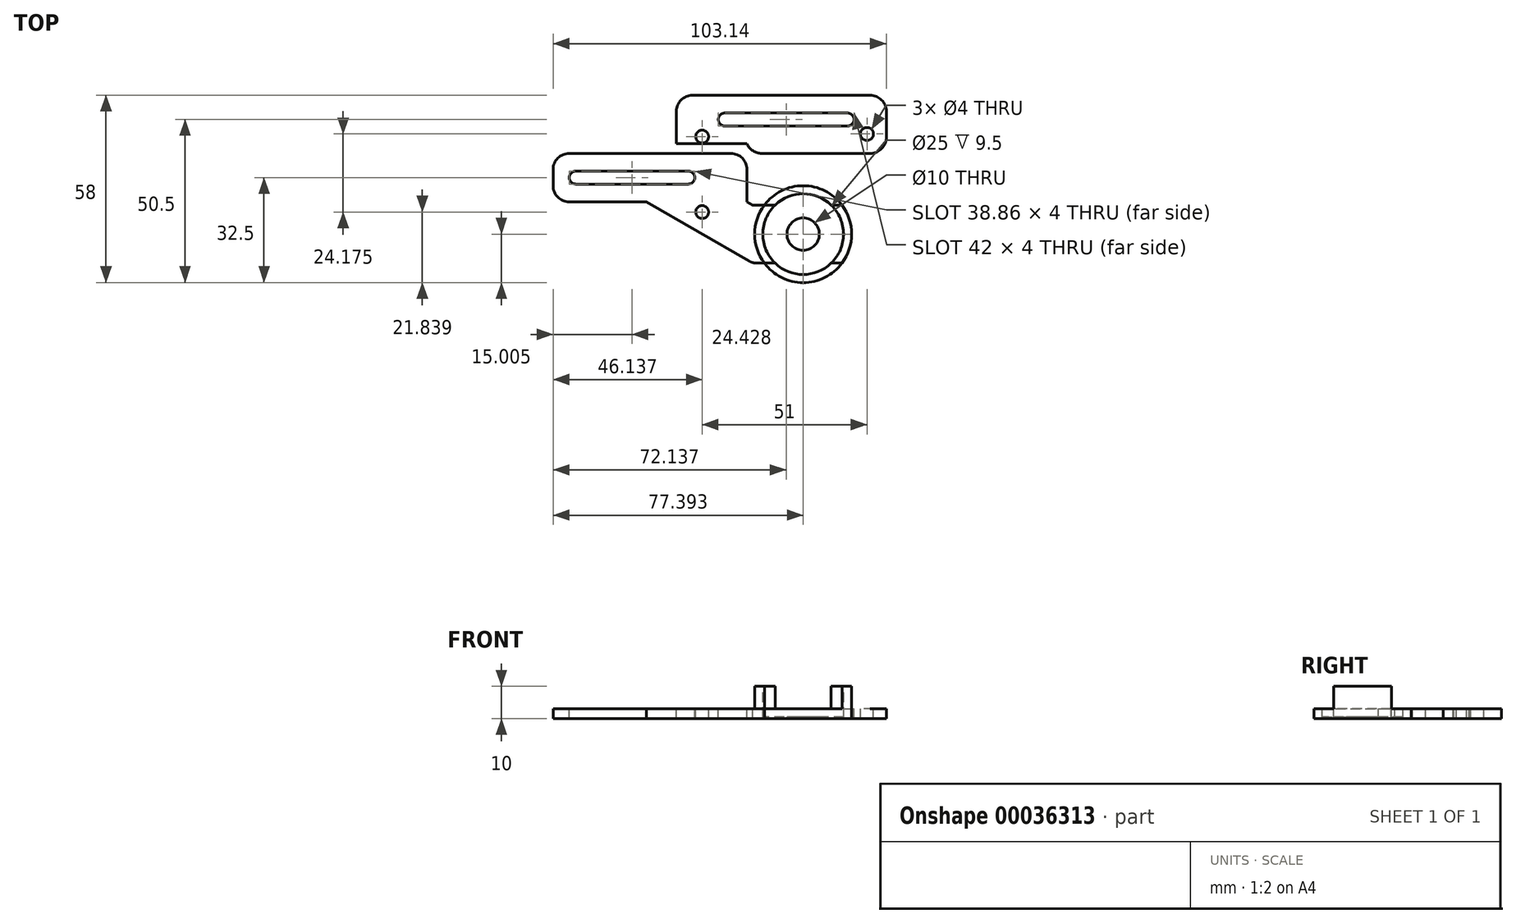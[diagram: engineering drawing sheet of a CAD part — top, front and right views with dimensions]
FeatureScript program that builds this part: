
annotation { "Feature Type Name" : "Feature", "Feature Type Description" : "" }
export const myFeature = defineFeature(function(context is Context, id is Id, definition is map)
    precondition{}
    {
        {
            var Q0;
            Q0=qCreatedBy(makeId("Top.planeOp"),FACE);
            var sketch = newSketch(context, id + "F0", { "sketchPlane" : qUnion([Q0])});
            skLineSegment(sketch, "E0.bottom", {"start": v(-30, 15) * mm, "end": v(30, 15) * mm});
            skLineSegment(sketch, "E0.top", {"start": v(-30, 0) * mm, "end": v(30, 0) * mm});
            skLineSegment(sketch, "E0.left", {"start": v(-30, 15) * mm, "end": v(-30, 0) * mm});
            skLineSegment(sketch, "E0.right", {"start": v(30, 15) * mm, "end": v(30, 0) * mm});
            skLineSegment(sketch, "E1", {"start": v(0, 0) * mm, "end": v(0, 15) * mm, "construction": true});
            skCircle(sketch, "E2", {"center": v(47.4, -10) * mm, "radius": 15 * mm});
            skLineSegment(sketch, "E3.left", {"start": v(31.72, -1) * mm, "end": v(31.72, -19) * mm});
            skLineSegment(sketch, "E3.right", {"start": v(47.4, -1) * mm, "end": v(47.4, -19) * mm});
            skCircle(sketch, "E4", {"center": v(47.4, -10) * mm, "radius": 12.5 * mm});
            skLineSegment(sketch, "E5", {"start": v(47.4, -10) * mm, "end": v(31.72, -10) * mm, "construction": true});
            skLineSegment(sketch, "E6", {"start": v(47.4, -1) * mm, "end": v(56.07, -1) * mm});
            skLineSegment(sketch, "E7", {"start": v(56.07, -1) * mm, "end": v(59.4, -1) * mm});
            skLineSegment(sketch, "E8", {"start": v(47.4, -19) * mm, "end": v(56.07, -19) * mm});
            skLineSegment(sketch, "E9", {"start": v(56.07, -19) * mm, "end": v(59.4, -19) * mm});
            skLineSegment(sketch, "E10", {"start": v(47.4, -1) * mm, "end": v(38.72, -1) * mm});
            skLineSegment(sketch, "E11", {"start": v(38.72, -1) * mm, "end": v(35.4, -1) * mm});
            skLineSegment(sketch, "E12", {"start": v(35.4, -1) * mm, "end": v(31.72, -1) * mm});
            skLineSegment(sketch, "E13", {"start": v(47.4, -19) * mm, "end": v(38.72, -19) * mm});
            skLineSegment(sketch, "E14", {"start": v(38.72, -19) * mm, "end": v(35.4, -19) * mm});
            skLineSegment(sketch, "E15", {"start": v(35.4, -19) * mm, "end": v(31.72, -19) * mm});
            skLineSegment(sketch, "E16", {"start": v(-30, 7.5) * mm, "end": v(0, 7.5) * mm, "construction": true});
            skLineSegment(sketch, "E17", {"start": v(0, 7.5) * mm, "end": v(30, 7.5) * mm, "construction": true});
            skLineSegment(sketch, "E18", {"start": v(-10, 7.5) * mm, "end": v(47.4, -10) * mm, "construction": true});
            skLineSegment(sketch, "E19", {"start": v(31.72, -19) * mm, "end": v(-1.15, 0) * mm});
            skLineSegment(sketch, "E20", {"start": v(31.72, -1) * mm, "end": v(30, 0) * mm});
            skLineSegment(sketch, "E21.bottom", {"start": v(30, 15) * mm, "end": v(8.14, 15) * mm});
            skLineSegment(sketch, "E21.top", {"start": v(30, 18) * mm, "end": v(8.14, 18) * mm});
            skLineSegment(sketch, "E21.left", {"start": v(30, 15) * mm, "end": v(30, 18) * mm});
            skLineSegment(sketch, "E21.right", {"start": v(8.14, 15) * mm, "end": v(8.14, 18) * mm});
            skLineSegment(sketch, "E22.bottom", {"start": v(8.14, 18) * mm, "end": v(73.14, 18) * mm});
            skLineSegment(sketch, "E22.top", {"start": v(8.14, 33) * mm, "end": v(73.14, 33) * mm});
            skLineSegment(sketch, "E22.left", {"start": v(8.14, 18) * mm, "end": v(8.14, 33) * mm});
            skLineSegment(sketch, "E22.right", {"start": v(73.14, 18) * mm, "end": v(73.14, 33) * mm});
            skCircle(sketch, "E23", {"center": v(-23, 7.5) * mm, "radius": 2 * mm});
            skCircle(sketch, "E24", {"center": v(11.86, 7.5) * mm, "radius": 2 * mm});
            skLineSegment(sketch, "E25", {"start": v(40.64, 33) * mm, "end": v(40.64, 25.5) * mm});
            skLineSegment(sketch, "E26", {"start": v(40.64, 25.5) * mm, "end": v(40.64, 18) * mm});
            skLineSegment(sketch, "E27", {"start": v(8.14, 25.5) * mm, "end": v(40.64, 25.5) * mm, "construction": true});
            skLineSegment(sketch, "E28", {"start": v(40.64, 25.5) * mm, "end": v(73.14, 25.5) * mm, "construction": true});
            skCircle(sketch, "E29", {"center": v(61.14, 25.5) * mm, "radius": 2 * mm});
            skCircle(sketch, "E30", {"center": v(23.14, 25.5) * mm, "radius": 2 * mm});
            skLineSegment(sketch, "E31", {"start": v(11.86, 7.5) * mm, "end": v(11.86, 9.5) * mm});
            skLineSegment(sketch, "E32", {"start": v(11.86, 7.5) * mm, "end": v(11.86, 5.5) * mm});
            skLineSegment(sketch, "E33", {"start": v(11.86, 5.5) * mm, "end": v(-23, 5.5) * mm});
            skLineSegment(sketch, "E34", {"start": v(-23, 5.5) * mm, "end": v(-23, 7.5) * mm});
            skLineSegment(sketch, "E35", {"start": v(11.86, 9.5) * mm, "end": v(-23, 9.5) * mm});
            skLineSegment(sketch, "E36", {"start": v(-23, 9.5) * mm, "end": v(-23, 7.5) * mm});
            skLineSegment(sketch, "E37", {"start": v(23.14, 25.5) * mm, "end": v(23.14, 23.5) * mm});
            skLineSegment(sketch, "E38", {"start": v(61.14, 23.5) * mm, "end": v(61.14, 25.5) * mm});
            skLineSegment(sketch, "E39", {"start": v(23.14, 25.5) * mm, "end": v(23.14, 27.5) * mm});
            skLineSegment(sketch, "E40", {"start": v(61.14, 27.5) * mm, "end": v(61.14, 25.5) * mm});
            skLineSegment(sketch, "E41", {"start": v(23.14, 23.5) * mm, "end": v(61.14, 23.5) * mm});
            skLineSegment(sketch, "E42", {"start": v(61.14, 27.5) * mm, "end": v(23.14, 27.5) * mm});
            skLineSegment(sketch, "E43", {"start": v(30, 15) * mm, "end": v(73.14, 15) * mm});
            skLineSegment(sketch, "E44", {"start": v(73.14, 15) * mm, "end": v(73.14, 18) * mm});
            skCircle(sketch, "E45", {"center": v(16.14, 20.22) * mm, "radius": 2 * mm});
            skCircle(sketch, "E46", {"center": v(67.14, 21.01) * mm, "radius": 2 * mm});
            skCircle(sketch, "E47", {"center": v(16.14, -3.16) * mm, "radius": 2 * mm});
            skSolve(sketch);
        }
        {
            var Q0;
            Q0=makeQuery(id+"F0.imprint","IMPRINT",FACE,{"disambiguationData":[TD([[makeQuery(id+"F0.imprint","IMPRINT",EDGE,{"derivedFrom":sQuery(id+"F0.wireOp",EDGE,"E3.right")}),-1.0]])]});
            var sketch = newSketch(context, id + "F1", { "sketchPlane" : qUnion([Q0])});
            skCircle(sketch, "E48", {"center": v(47.4, -10) * mm, "radius": 5 * mm});
            skSolve(sketch);
        }
        {
            var Q0;
            Q0=makeQuery(id+"F0.imprint","IMPRINT",FACE,{"disambiguationData":[TD([[makeQuery(id+"F0.imprint","IMPRINT",EDGE,{"derivedFrom":sQuery(id+"F0.wireOp",EDGE,"E0.bottom")}),-1.0]])]});
            var Q1;
            Q1=makeQuery(id+"F0.imprint","IMPRINT",FACE,{"disambiguationData":[TD([[makeQuery(id+"F0.imprint","IMPRINT",EDGE,{"derivedFrom":sQuery(id+"F0.wireOp",EDGE,"E3.left")}),-1.0]])]});
            var Q2;
            Q2=makeQuery(id+"F0.imprint","IMPRINT",FACE,{"disambiguationData":[TD([[makeQuery(id+"F0.imprint","IMPRINT",EDGE,{"derivedFrom":sQuery(id+"F0.wireOp",EDGE,"E22.top")}),-1.0]])]});
            var Q3;
            Q3=makeQuery(id+"F0.imprint","IMPRINT",FACE,{"disambiguationData":[TD([[makeQuery(id+"F0.imprint","IMPRINT",EDGE,{"derivedFrom":sQuery(id+"F0.wireOp",EDGE,"E21.bottom")}),-1.0]])]});
            var Q4;
            Q4=makeQuery(id+"F0.imprint","IMPRINT",FACE,{"disambiguationData":[TD([[makeQuery(id+"F0.imprint","IMPRINT",EDGE,{"derivedFrom":sQuery(id+"F0.wireOp",EDGE,"E3.left")}),1.0]])]});
            var Q5;
            {var subQ1=sQuery(id+"F0.wireOp",EDGE,"E11");Q5=makeQuery(id+"F0.imprint","IMPRINT",FACE,{"disambiguationData":[TD([[makeQuery(id+"F0.imprint","IMPRINT",EDGE,{"derivedFrom":subQ1}),1.0]])]});}
            var Q6;
            Q6=makeQuery(id+"F0.imprint","IMPRINT",FACE,{"disambiguationData":[TD([[makeQuery(id+"F0.imprint","IMPRINT",EDGE,{"derivedFrom":sQuery(id+"F0.wireOp",EDGE,"E3.right")}),-1.0]])]});
            var Q7;
            {var subQ1=sQuery(id+"F0.wireOp",EDGE,"E6");Q7=makeQuery(id+"F0.imprint","IMPRINT",FACE,{"disambiguationData":[TD([[makeQuery(id+"F0.imprint","IMPRINT",EDGE,{"derivedFrom":subQ1}),1.0]])]});}
            var Q8;
            Q8=makeQuery(id+"F0.imprint","IMPRINT",FACE,{"disambiguationData":[TD([[makeQuery(id+"F0.imprint","IMPRINT",EDGE,{"derivedFrom":sQuery(id+"F0.wireOp",EDGE,"E3.right")}),1.0]])]});
            var Q9;
            {var subQ1=sQuery(id+"F0.wireOp",EDGE,"E7");Q9=makeQuery(id+"F0.imprint","IMPRINT",FACE,{"disambiguationData":[TD([[makeQuery(id+"F0.imprint","IMPRINT",EDGE,{"derivedFrom":subQ1}),-1.0]])]});}
            var Q10;
            {var subQ1=sQuery(id+"F0.wireOp",EDGE,"E9");Q10=makeQuery(id+"F0.imprint","IMPRINT",FACE,{"disambiguationData":[TD([[makeQuery(id+"F0.imprint","IMPRINT",EDGE,{"derivedFrom":subQ1}),-1.0]])]});}
            var Q11;
            {var subQ1=sQuery(id+"F0.wireOp",EDGE,"E8");Q11=makeQuery(id+"F0.imprint","IMPRINT",FACE,{"disambiguationData":[TD([[makeQuery(id+"F0.imprint","IMPRINT",EDGE,{"derivedFrom":subQ1}),-1.0]])]});}
            var Q12;
            {var subQ1=sQuery(id+"F0.wireOp",EDGE,"E7");Q12=makeQuery(id+"F0.imprint","IMPRINT",FACE,{"disambiguationData":[TD([[makeQuery(id+"F0.imprint","IMPRINT",EDGE,{"derivedFrom":subQ1}),1.0]])]});}
            var Q13;
            {var subQ1=sQuery(id+"F0.wireOp",EDGE,"E33");Q13=makeQuery(id+"F0.imprint","IMPRINT",FACE,{"disambiguationData":[TD([[makeQuery(id+"F0.imprint","IMPRINT",EDGE,{"derivedFrom":subQ1}),-1.0]])]});}
            var Q14;
            {var subQ1=sQuery(id+"F0.wireOp",EDGE,"E31");Q14=makeQuery(id+"F0.imprint","IMPRINT",FACE,{"disambiguationData":[TD([[makeQuery(id+"F0.imprint","IMPRINT",EDGE,{"derivedFrom":subQ1}),1.0]])]});}
            var Q15;
            {var subQ1=sQuery(id+"F0.wireOp",EDGE,"E31");Q15=makeQuery(id+"F0.imprint","IMPRINT",FACE,{"disambiguationData":[TD([[makeQuery(id+"F0.imprint","IMPRINT",EDGE,{"derivedFrom":subQ1}),-1.0]])]});}
            var Q16;
            {var subQ1=sQuery(id+"F0.wireOp",EDGE,"E34");Q16=makeQuery(id+"F0.imprint","IMPRINT",FACE,{"disambiguationData":[TD([[makeQuery(id+"F0.imprint","IMPRINT",EDGE,{"derivedFrom":subQ1}),1.0]])]});}
            var Q17;
            {var subQ1=sQuery(id+"F0.wireOp",EDGE,"E34");Q17=makeQuery(id+"F0.imprint","IMPRINT",FACE,{"disambiguationData":[TD([[makeQuery(id+"F0.imprint","IMPRINT",EDGE,{"derivedFrom":subQ1}),-1.0]])]});}
            var Q18;
            {var subQ1=sQuery(id+"F0.wireOp",EDGE,"E37");Q18=makeQuery(id+"F0.imprint","IMPRINT",FACE,{"disambiguationData":[TD([[makeQuery(id+"F0.imprint","IMPRINT",EDGE,{"derivedFrom":subQ1}),-1.0]])]});}
            var Q19;
            {var subQ1=sQuery(id+"F0.wireOp",EDGE,"E37");Q19=makeQuery(id+"F0.imprint","IMPRINT",FACE,{"disambiguationData":[TD([[makeQuery(id+"F0.imprint","IMPRINT",EDGE,{"derivedFrom":subQ1}),1.0]])]});}
            var Q20;
            {var subQ1=sQuery(id+"F0.wireOp",EDGE,"E41");Q20=makeQuery(id+"F0.imprint","IMPRINT",FACE,{"disambiguationData":[TD([[makeQuery(id+"F0.imprint","IMPRINT",EDGE,{"derivedFrom":subQ1}),1.0]])]});}
            var Q21;
            {var subQ1=sQuery(id+"F0.wireOp",EDGE,"E38");Q21=makeQuery(id+"F0.imprint","IMPRINT",FACE,{"disambiguationData":[TD([[makeQuery(id+"F0.imprint","IMPRINT",EDGE,{"derivedFrom":subQ1}),1.0]])]});}
            var Q22;
            {var subQ1=sQuery(id+"F0.wireOp",EDGE,"E38");Q22=makeQuery(id+"F0.imprint","IMPRINT",FACE,{"disambiguationData":[TD([[makeQuery(id+"F0.imprint","IMPRINT",EDGE,{"derivedFrom":subQ1}),-1.0]])]});}
            var Q23;
            {var subQ13=sQuery(id+"F0.wireOp",EDGE,"E22.left");Q23=makeQuery(id+"F0.imprint","IMPRINT",FACE,{"disambiguationData":[TD([[makeQuery(id+"F0.imprint","IMPRINT",EDGE,{"derivedFrom":subQ13}),-1.0]])]});}
            var Q24;
            {var subQ3=sQuery(id+"F0.wireOp",EDGE,"E21.left");Q24=makeQuery(id+"F0.imprint","IMPRINT",FACE,{"disambiguationData":[TD([[makeQuery(id+"F0.imprint","IMPRINT",EDGE,{"derivedFrom":subQ3}),-1.0]])]});}
            extrude(context, id + "F2", {"entities" : qUnion([Q0, Q1, Q2, Q3, Q4, Q5, Q6, Q7, Q8, Q9, Q10, Q11, Q12, Q13, Q14, Q15, Q16, Q17, Q18, Q19, Q20, Q21, Q22, Q23, Q24]), "oppositeDirection" : true, "depth" : 3 * mm});
        }
        {
            var Q0;
            {var subQ1=sQuery(id+"F0.wireOp",EDGE,"E6");Q0=makeQuery(id+"F0.imprint","IMPRINT",FACE,{"disambiguationData":[TD([[makeQuery(id+"F0.imprint","IMPRINT",EDGE,{"derivedFrom":subQ1}),1.0]])]});}
            var Q1;
            Q1=makeQuery(id+"F0.imprint","IMPRINT",FACE,{"disambiguationData":[TD([[makeQuery(id+"F0.imprint","IMPRINT",EDGE,{"derivedFrom":sQuery(id+"F0.wireOp",EDGE,"E3.right")}),-1.0]])]});
            var Q2;
            Q2=makeQuery(id+"F0.imprint","IMPRINT",FACE,{"disambiguationData":[TD([[makeQuery(id+"F0.imprint","IMPRINT",EDGE,{"derivedFrom":sQuery(id+"F0.wireOp",EDGE,"E3.right")}),1.0]])]});
            var Q3;
            {var subQ1=sQuery(id+"F0.wireOp",EDGE,"E8");Q3=makeQuery(id+"F0.imprint","IMPRINT",FACE,{"disambiguationData":[TD([[makeQuery(id+"F0.imprint","IMPRINT",EDGE,{"derivedFrom":subQ1}),-1.0]])]});}
            extrude(context, id + "F3", {"entities" : qUnion([Q0, Q1, Q2, Q3]), "operationType" : NewBodyOperationType.REMOVE, "oppositeDirection" : true, "depth" : 2.5 * mm});
        }
        {
            var Q0;
            {var subQ0=makeQuery(id+"F0.imprint","IMPRINT",EDGE,{"derivedFrom":sQuery(id+"F0.wireOp",EDGE,"E3.right")});var subQ1=sQuery(id+"F1.wireOp",EDGE,"E48");var subQ3=makeQuery(id+"F1.imprint","INTERSECT",VERTEX,{"disambiguationData":[OD(0.0)],"derivedFrom":[subQ0,subQ1]});Q0=makeQuery(id+"F1.imprint","IMPRINT",FACE,{"disambiguationData":[TD([[makeQuery(id+"F1.imprint","IMPRINT",EDGE,{"disambiguationData":[TD([[subQ3,-1.0]])],"derivedFrom":subQ1}),1.0]])]});}
            var Q1;
            {var subQ0=makeQuery(id+"F0.imprint","IMPRINT",EDGE,{"derivedFrom":sQuery(id+"F0.wireOp",EDGE,"E3.right")});var subQ1=sQuery(id+"F1.wireOp",EDGE,"E48");var subQ3=makeQuery(id+"F1.imprint","INTERSECT",VERTEX,{"disambiguationData":[OD(0.0)],"derivedFrom":[subQ0,subQ1]});Q1=makeQuery(id+"F1.imprint","IMPRINT",FACE,{"disambiguationData":[TD([[makeQuery(id+"F1.imprint","IMPRINT",EDGE,{"disambiguationData":[TD([[subQ3,1.0]])],"derivedFrom":subQ1}),1.0]])]});}
            extrude(context, id + "F4", {"entities" : qUnion([Q0, Q1]), "operationType" : NewBodyOperationType.REMOVE, "endBound" : BoundingType.THROUGH_ALL, "oppositeDirection" : true, "depth" : 25 * mm});
        }
        {
            var Q0;
            {var subQ1=sQuery(id+"F0.wireOp",EDGE,"E37");Q0=makeQuery(id+"F0.imprint","IMPRINT",FACE,{"disambiguationData":[TD([[makeQuery(id+"F0.imprint","IMPRINT",EDGE,{"derivedFrom":subQ1}),-1.0]])]});}
            var Q1;
            {var subQ1=sQuery(id+"F0.wireOp",EDGE,"E37");Q1=makeQuery(id+"F0.imprint","IMPRINT",FACE,{"disambiguationData":[TD([[makeQuery(id+"F0.imprint","IMPRINT",EDGE,{"derivedFrom":subQ1}),1.0]])]});}
            var Q2;
            {var subQ1=sQuery(id+"F0.wireOp",EDGE,"E41");Q2=makeQuery(id+"F0.imprint","IMPRINT",FACE,{"disambiguationData":[TD([[makeQuery(id+"F0.imprint","IMPRINT",EDGE,{"derivedFrom":subQ1}),1.0]])]});}
            var Q3;
            {var subQ1=sQuery(id+"F0.wireOp",EDGE,"E38");Q3=makeQuery(id+"F0.imprint","IMPRINT",FACE,{"disambiguationData":[TD([[makeQuery(id+"F0.imprint","IMPRINT",EDGE,{"derivedFrom":subQ1}),1.0]])]});}
            var Q4;
            {var subQ1=sQuery(id+"F0.wireOp",EDGE,"E38");Q4=makeQuery(id+"F0.imprint","IMPRINT",FACE,{"disambiguationData":[TD([[makeQuery(id+"F0.imprint","IMPRINT",EDGE,{"derivedFrom":subQ1}),-1.0]])]});}
            var Q5;
            {var subQ1=sQuery(id+"F0.wireOp",EDGE,"E31");Q5=makeQuery(id+"F0.imprint","IMPRINT",FACE,{"disambiguationData":[TD([[makeQuery(id+"F0.imprint","IMPRINT",EDGE,{"derivedFrom":subQ1}),-1.0]])]});}
            var Q6;
            {var subQ1=sQuery(id+"F0.wireOp",EDGE,"E31");Q6=makeQuery(id+"F0.imprint","IMPRINT",FACE,{"disambiguationData":[TD([[makeQuery(id+"F0.imprint","IMPRINT",EDGE,{"derivedFrom":subQ1}),1.0]])]});}
            var Q7;
            {var subQ1=sQuery(id+"F0.wireOp",EDGE,"E33");Q7=makeQuery(id+"F0.imprint","IMPRINT",FACE,{"disambiguationData":[TD([[makeQuery(id+"F0.imprint","IMPRINT",EDGE,{"derivedFrom":subQ1}),-1.0]])]});}
            var Q8;
            {var subQ1=sQuery(id+"F0.wireOp",EDGE,"E34");Q8=makeQuery(id+"F0.imprint","IMPRINT",FACE,{"disambiguationData":[TD([[makeQuery(id+"F0.imprint","IMPRINT",EDGE,{"derivedFrom":subQ1}),-1.0]])]});}
            var Q9;
            {var subQ1=sQuery(id+"F0.wireOp",EDGE,"E34");Q9=makeQuery(id+"F0.imprint","IMPRINT",FACE,{"disambiguationData":[TD([[makeQuery(id+"F0.imprint","IMPRINT",EDGE,{"derivedFrom":subQ1}),1.0]])]});}
            extrude(context, id + "F5", {"entities" : qUnion([Q0, Q1, Q2, Q3, Q4, Q5, Q6, Q7, Q8, Q9]), "operationType" : NewBodyOperationType.REMOVE, "endBound" : BoundingType.UP_TO_NEXT, "oppositeDirection" : true, "depth" : 25 * mm});
        }
        {
            var Q0;
            Q0=makeQuery(id+"F2.opExtrude","SWEPT_EDGE",EDGE,{"disambiguationData":[OSD([sQuery(id+"F0.wireOp",EDGE,"E22.top"),sQuery(id+"F0.wireOp",EDGE,"E22.left")])]});
            var Q1;
            Q1=makeQuery(id+"F2.opExtrude","SWEPT_EDGE",EDGE,{"disambiguationData":[OSD([sQuery(id+"F0.wireOp",EDGE,"E0.bottom"),sQuery(id+"F0.wireOp",EDGE,"E0.left")])]});
            var Q2;
            Q2=makeQuery(id+"F2.opExtrude","SWEPT_EDGE",EDGE,{"disambiguationData":[OSD([sQuery(id+"F0.wireOp",EDGE,"E0.top"),sQuery(id+"F0.wireOp",EDGE,"E0.left")])]});
            var Q3;
            Q3=makeQuery(id+"F2.opExtrude","SWEPT_EDGE",EDGE,{"disambiguationData":[OSD([sQuery(id+"F0.wireOp",EDGE,"E3.left"),sQuery(id+"F0.wireOp",EDGE,"E15"),sQuery(id+"F0.wireOp",EDGE,"E19")])]});
            var Q4;
            Q4=makeQuery(id+"F2.opExtrude","SWEPT_EDGE",EDGE,{"disambiguationData":[OSD([sQuery(id+"F0.wireOp",EDGE,"E22.top"),sQuery(id+"F0.wireOp",EDGE,"E22.right")])]});
            var Q5;
            Q5=makeQuery(id+"F2.opExtrude","SWEPT_EDGE",EDGE,{"disambiguationData":[OSD([sQuery(id+"F0.wireOp",EDGE,"E43"),sQuery(id+"F0.wireOp",EDGE,"E44")])]});
            var Q6;
            Q6=makeQuery(id+"F2.opExtrude","SWEPT_EDGE",EDGE,{"disambiguationData":[OSD([sQuery(id+"F0.wireOp",EDGE,"E0.right"),sQuery(id+"F0.wireOp",EDGE,"E21.bottom"),sQuery(id+"F0.wireOp",EDGE,"E21.left"),sQuery(id+"F0.wireOp",EDGE,"E43")])]});
            var Q7;
            Q7=makeQuery(id+"F2.opExtrude","SWEPT_EDGE",EDGE,{"disambiguationData":[OSD([sQuery(id+"F0.wireOp",EDGE,"E0.bottom"),sQuery(id+"F0.wireOp",EDGE,"E21.bottom"),sQuery(id+"F0.wireOp",EDGE,"E21.right")])]});
            fillet(context, id + "F6", {"entities" : qUnion([Q0, Q1, Q2, Q3, Q4, Q5, Q6, Q7]), "radius" : 5 * mm, "tangentPropagation" : true, "allowEdgeOverflow" : false});
        }
        {
            var Q0;
            {var subQ1=sQuery(id+"F0.wireOp",EDGE,"E7");Q0=makeQuery(id+"F0.imprint","IMPRINT",FACE,{"disambiguationData":[TD([[makeQuery(id+"F0.imprint","IMPRINT",EDGE,{"derivedFrom":subQ1}),-1.0]])]});}
            var Q1;
            {var subQ1=sQuery(id+"F0.wireOp",EDGE,"E11");Q1=makeQuery(id+"F0.imprint","IMPRINT",FACE,{"disambiguationData":[TD([[makeQuery(id+"F0.imprint","IMPRINT",EDGE,{"derivedFrom":subQ1}),1.0]])]});}
            extrude(context, id + "F7", {"entities" : qUnion([Q0, Q1]), "operationType" : NewBodyOperationType.ADD, "depth" : 7 * mm});
        }
    });
